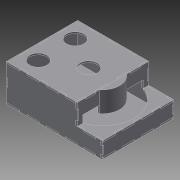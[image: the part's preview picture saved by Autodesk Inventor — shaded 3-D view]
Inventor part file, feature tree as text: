
AUTODESK INVENTOR PART (.ipt)
format: ipt  version: 2021.3 (Build 253353000, 353)  size: 879,616 bytes
history: native  units: mm
features: projected_geometry x45, extrude x25, sketch x25, other x11, mirror x4
ambient origin geometry x8: Origin, YZ Plane, XZ Plane, XY Plane, X Axis, Y Axis, Z Axis, Center Point
bodies: Body1 (feature_tree), Body2 (feature_tree), Body3 (feature_tree), Body4 (feature_tree), Body5 (feature_tree), Body6 (feature_tree), Body7 (feature_tree), Body8 (feature_tree), Body9 (feature_tree)
feature tree (110):
  other  "Основание_нижнее"
  extrude  "Выдавливание1"  Depth=6.0mm TaperAngle=0.0deg
  sketch  "Эскиз2"
  extrude  "Выдавливание2"  Depth=6.0mm
  extrude  "Выдавливание3"  Depth=6.0mm
  extrude  "Выдавливание4"  Depth=150.0mm TaperAngle=0.0deg
  extrude  "Выдавливание5"  Depth=150.0mm TaperAngle=0.0deg
  extrude  "Выдавливание6"  Depth=47.0mm
  extrude  "Выдавливание7"  Depth=47.0mm
  extrude  "Выдавливание8"  TaperAngle=0.0deg  [1 undecoded]
  mirror  "Зеркальное отражение2"
  other  "РабПлоскость1"
  mirror  "Зеркальное отражение3"
  mirror  "Зеркальное отражение4"
  mirror  "Зеркальное отражение5"
  sketch  "Эскиз20"
  extrude  "Выдавливание20"  TaperAngle=0.0deg  [1 undecoded]
  extrude  "Выдавливание9"  TaperAngle=0.0deg  [1 undecoded]
  extrude  "Выдавливание21"  Depth=30.0mm
  extrude  "Выдавливание22"  Depth=6.0mm
  extrude  "Выдавливание23"  TaperAngle=0.0deg  [1 undecoded]
  extrude  "Выдавливание24"  TaperAngle=0.0deg  [1 undecoded]
  extrude  "Выдавливание25"  Depth=6.0mm TaperAngle=0.0deg
  extrude  "Выдавливание26"  Depth=49.0mm
  extrude  "Выдавливание27"  Depth=49.0mm
  extrude  "Выдавливание28"  Depth=49.0mm
  extrude  "Выдавливание29"  Depth=49.0mm
  extrude  "Выдавливание30"  Depth=49.0mm
  extrude  "Выдавливание31"  Depth=30.0mm
  extrude  "Выдавливание32"  Depth=390.0mm
  extrude  "Выдавливание34"  Depth=290.0mm
  extrude  "Выдавливание35"  Depth=145.0mm
  extrude  "Выдавливание36"  Depth=53.0mm
  sketch  "Эскиз1"
  other  "Стенка_боковая_1"
  other  "Стенка_задняя"
  sketch  "Эскиз3"
  sketch  "Эскиз4"
  projected_geometry  "Спроецированная петля1"
  projected_geometry  "Спроецированная петля2"
  projected_geometry  "Спроецированная петля3"
  sketch  "Эскиз5"
  projected_geometry  "Спроецированная петля4"
  projected_geometry  "Спроецированная петля5"
  projected_geometry  "Спроецированная петля6"
  projected_geometry  "Спроецированная петля7"
  sketch  "Эскиз6"
  sketch  "Эскиз7"
  other  "Шаблон Стенка_боковая_1:2"
  other  "Стенка боковая_2"
  sketch  "Эскиз8"
  projected_geometry  "Спроецированная петля10"
  other  "Основание_верхнее"
  projected_geometry  "Спроецированная петля17"
  projected_geometry  "Спроецированная петля18"
  projected_geometry  "Спроецированная петля19"
  sketch  "Эскиз21"
  sketch  "Эскиз22"
  other  "Стенка_торцевая_передняя"
  sketch  "Эскиз23"
  projected_geometry  "Спроецированная петля20"
  projected_geometry  "Спроецированная петля21"
  projected_geometry  "Спроецированная петля22"
  projected_geometry  "Спроецированная петля23"
  projected_geometry  "Спроецированная петля24"
  sketch  "Эскиз24"
  projected_geometry  "Спроецированная петля25"
  projected_geometry  "Спроецированная петля26"
  sketch  "Эскиз25"
  other  "Основание_малое"
  projected_geometry  "Спроецированная петля27"
  projected_geometry  "Спроецированная петля28"
  projected_geometry  "Спроецированная петля29"
  projected_geometry  "Спроецированная петля30"
  projected_geometry  "Спроецированная петля31"
  projected_geometry  "Спроецированная петля32"
  projected_geometry  "Спроецированная петля33"
  projected_geometry  "Спроецированная петля34"
  projected_geometry  "Спроецированная петля35"
  sketch  "Эскиз27"
  projected_geometry  "Спроецированная петля36"
  projected_geometry  "Спроецированная петля37"
  sketch  "Эскиз28"
  projected_geometry  "Спроецированная петля38"
  projected_geometry  "Спроецированная петля39"
  projected_geometry  "Спроецированная петля40"
  projected_geometry  "Спроецированная петля41"
  sketch  "Эскиз29"
  projected_geometry  "Спроецированная петля42"
  projected_geometry  "Спроецированная петля43"
  projected_geometry  "Спроецированная петля44"
  sketch  "Эскиз30"
  other  "Стенка_передняя"
  sketch  "Эскиз31"
  projected_geometry  "Спроецированная петля45"
  projected_geometry  "Спроецированная петля46"
  projected_geometry  "Спроецированная петля47"
  sketch  "Эскиз32"
  sketch  "Эскиз33"
  sketch  "Эскиз34"
  projected_geometry  "Спроецированная петля54"
  projected_geometry  "Спроецированная петля55"
  projected_geometry  "Спроецированная петля56"
  projected_geometry  "Спроецированная петля57"
  projected_geometry  "Спроецированная петля58"
  projected_geometry  "Спроецированная петля59"
  sketch  "Эскиз36"
  other  "Обтекатель"
  sketch  "Эскиз37"
  sketch  "Эскиз38"
note: 5 required parameter values undecoded (feature->parameter linkage not recoverable at this tier; creation-order binding heuristic only, values carry confidence <= 0.55)
